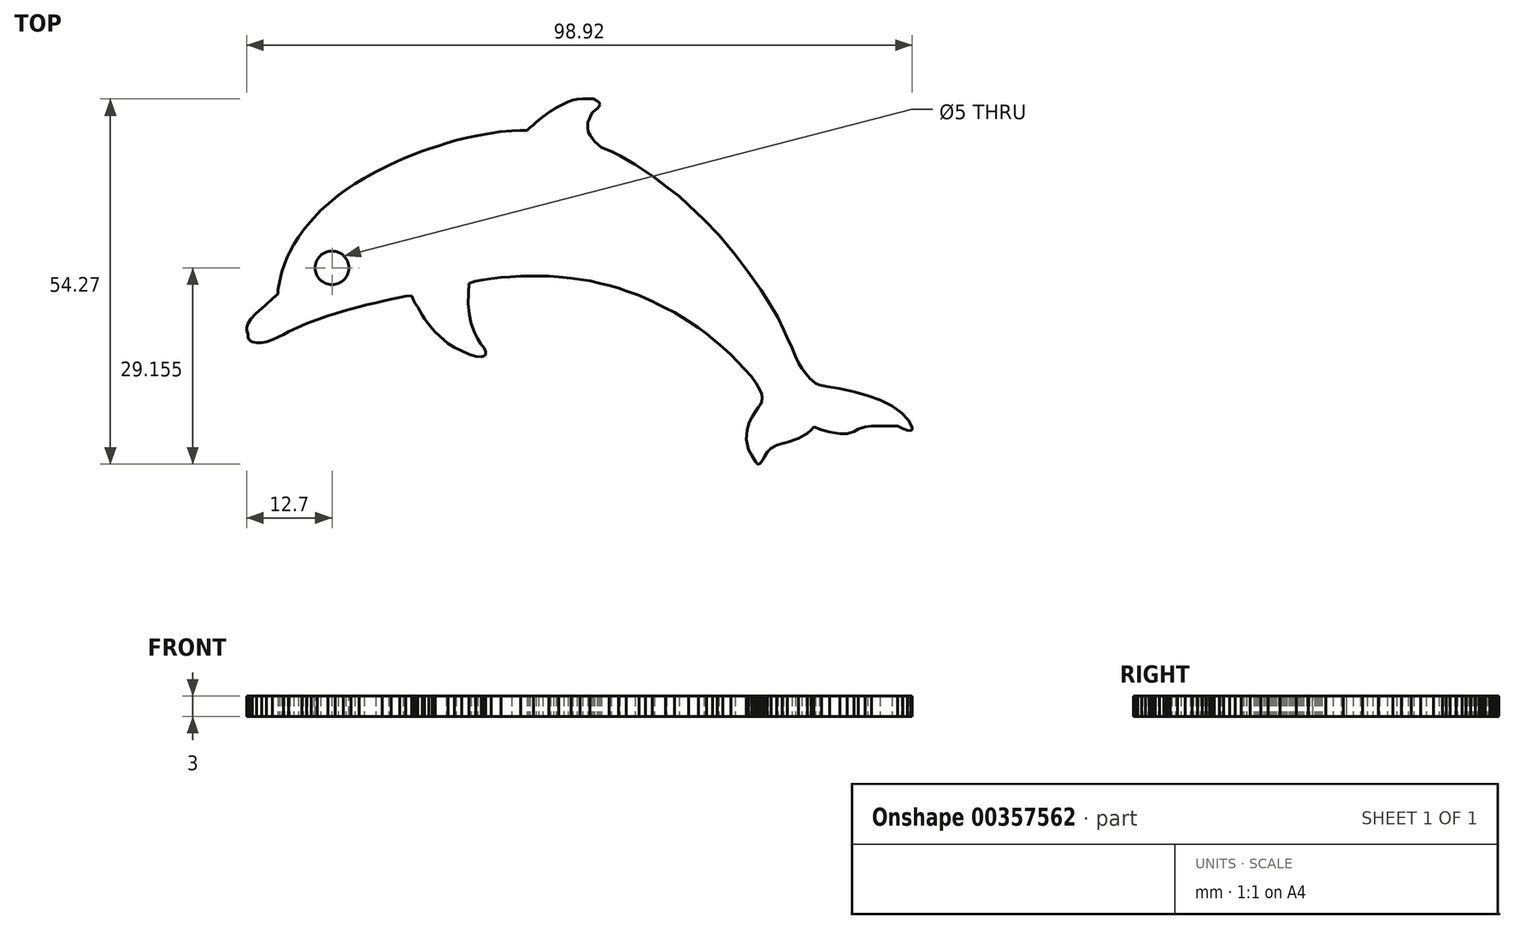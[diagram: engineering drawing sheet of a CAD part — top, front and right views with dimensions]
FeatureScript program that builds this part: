
annotation { "Feature Type Name" : "Feature", "Feature Type Description" : "" }
export const myFeature = defineFeature(function(context is Context, id is Id, definition is map)
    precondition{}
    {
        {
            var Q0;
            Q0=qCreatedBy(makeId("Top.planeOp"),FACE);
            var sketch = newSketch(context, id + "F0", { "sketchPlane" : qUnion([Q0])});
            skLineSegment(sketch, "E0.bottom", {"start": v(0, 0) * mm, "end": v(-99.99, 0) * mm});
            skLineSegment(sketch, "E1", {"start": v(-15.33, 6.38) * mm, "end": v(-14.23, 5.94) * mm});
            skLineSegment(sketch, "E2", {"start": v(-14.23, 5.94) * mm, "end": v(-13.02, 5.63) * mm});
            skLineSegment(sketch, "E3", {"start": v(-13.02, 5.63) * mm, "end": v(-11.47, 5.39) * mm});
            skLineSegment(sketch, "E4", {"start": v(-11.47, 5.39) * mm, "end": v(-10.37, 5.39) * mm});
            skLineSegment(sketch, "E5", {"start": v(-10.37, 5.39) * mm, "end": v(-9.38, 5.72) * mm});
            skLineSegment(sketch, "E6", {"start": v(-9.38, 5.72) * mm, "end": v(-8.72, 6.1) * mm});
            skLineSegment(sketch, "E7", {"start": v(-8.72, 6.1) * mm, "end": v(-7.72, 6.4) * mm});
            skLineSegment(sketch, "E8", {"start": v(-7.72, 6.4) * mm, "end": v(-6.76, 6.54) * mm});
            skLineSegment(sketch, "E9", {"start": v(-6.76, 6.54) * mm, "end": v(-5.65, 6.54) * mm});
            skLineSegment(sketch, "E10", {"start": v(-5.65, 6.54) * mm, "end": v(-2.9, 6.54) * mm});
            skPoint(sketch, "E10.endSnap0", {"position": v(-6.2, 6.54) * mm});
            skLineSegment(sketch, "E11", {"start": v(-2.9, 6.54) * mm, "end": v(-2.14, 6.17) * mm});
            skLineSegment(sketch, "E12", {"start": v(-2.14, 6.17) * mm, "end": v(-1.43, 5.9) * mm});
            skLineSegment(sketch, "E13", {"start": v(-1.43, 5.9) * mm, "end": v(-0.96, 5.8) * mm});
            skLineSegment(sketch, "E14", {"start": v(-0.96, 5.8) * mm, "end": v(-0.72, 5.96) * mm});
            skLineSegment(sketch, "E15", {"start": v(-0.72, 5.96) * mm, "end": v(-0.72, 6.33) * mm});
            skLineSegment(sketch, "E16", {"start": v(-0.72, 6.33) * mm, "end": v(-1.34, 7.4) * mm});
            skLineSegment(sketch, "E17", {"start": v(-1.34, 7.4) * mm, "end": v(-2.34, 8.52) * mm});
            skLineSegment(sketch, "E18", {"start": v(-2.34, 8.52) * mm, "end": v(-3.76, 9.53) * mm});
            skLineSegment(sketch, "E19", {"start": v(-3.76, 9.53) * mm, "end": v(-5.5, 10.4) * mm});
            skLineSegment(sketch, "E20", {"start": v(-5.5, 10.4) * mm, "end": v(-7.33, 11.05) * mm});
            skLineSegment(sketch, "E21", {"start": v(-7.33, 11.05) * mm, "end": v(-9.32, 11.63) * mm});
            skLineSegment(sketch, "E22", {"start": v(-9.32, 11.63) * mm, "end": v(-11.6, 12.13) * mm});
            skLineSegment(sketch, "E23", {"start": v(-11.6, 12.13) * mm, "end": v(-13.27, 12.4) * mm});
            skLineSegment(sketch, "E24", {"start": v(-13.27, 12.4) * mm, "end": v(-14.54, 12.6) * mm});
            skLineSegment(sketch, "E25", {"start": v(-14.54, 12.6) * mm, "end": v(-15.08, 12.86) * mm});
            skLineSegment(sketch, "E26", {"start": v(-15.08, 12.86) * mm, "end": v(-15.9, 13.6) * mm});
            skLineSegment(sketch, "E27", {"start": v(-15.9, 13.6) * mm, "end": v(-16.5, 14.26) * mm});
            skLineSegment(sketch, "E28", {"start": v(-16.5, 14.26) * mm, "end": v(-17.1, 15.11) * mm});
            skLineSegment(sketch, "E29", {"start": v(-17.1, 15.11) * mm, "end": v(-17.61, 15.95) * mm});
            skLineSegment(sketch, "E30", {"start": v(-17.61, 15.95) * mm, "end": v(-18.05, 16.88) * mm});
            skLineSegment(sketch, "E31", {"start": v(-18.05, 16.88) * mm, "end": v(-18.59, 18.16) * mm});
            skLineSegment(sketch, "E32", {"start": v(-18.59, 18.16) * mm, "end": v(-19.32, 19.77) * mm});
            skLineSegment(sketch, "E33", {"start": v(-19.32, 19.77) * mm, "end": v(-19.89, 20.87) * mm});
            skLineSegment(sketch, "E34", {"start": v(-19.89, 20.87) * mm, "end": v(-20.7, 22.66) * mm});
            skLineSegment(sketch, "E35", {"start": v(-20.7, 22.66) * mm, "end": v(-22.15, 25.05) * mm});
            skLineSegment(sketch, "E36", {"start": v(-22.15, 25.05) * mm, "end": v(-23.23, 26.8) * mm});
            skLineSegment(sketch, "E37", {"start": v(-23.23, 26.8) * mm, "end": v(-25.1, 29.44) * mm});
            skLineSegment(sketch, "E38", {"start": v(-25.1, 29.44) * mm, "end": v(-27, 32.02) * mm});
            skLineSegment(sketch, "E39", {"start": v(-27, 32.02) * mm, "end": v(-29.44, 34.91) * mm});
            skLineSegment(sketch, "E40", {"start": v(-29.44, 34.91) * mm, "end": v(-31.68, 37.22) * mm});
            skLineSegment(sketch, "E41", {"start": v(-31.68, 37.22) * mm, "end": v(-33.94, 39.38) * mm});
            skLineSegment(sketch, "E42", {"start": v(-33.94, 39.38) * mm, "end": v(-35.38, 40.67) * mm});
            skLineSegment(sketch, "E43", {"start": v(-35.38, 40.67) * mm, "end": v(-37.23, 42.1) * mm});
            skLineSegment(sketch, "E44", {"start": v(-37.23, 42.1) * mm, "end": v(-39, 43.51) * mm});
            skLineSegment(sketch, "E45", {"start": v(-39, 43.51) * mm, "end": v(-41.91, 45.4) * mm});
            skLineSegment(sketch, "E46", {"start": v(-41.91, 45.4) * mm, "end": v(-44.16, 46.74) * mm});
            skLineSegment(sketch, "E47", {"start": v(-44.16, 46.74) * mm, "end": v(-45.42, 47.36) * mm});
            skLineSegment(sketch, "E48", {"start": v(-45.42, 47.36) * mm, "end": v(-46.9, 47.9) * mm});
            skLineSegment(sketch, "E49", {"start": v(-46.9, 47.9) * mm, "end": v(-47.92, 48.82) * mm});
            skLineSegment(sketch, "E50", {"start": v(-47.92, 48.82) * mm, "end": v(-48.58, 49.7) * mm});
            skLineSegment(sketch, "E51", {"start": v(-48.58, 49.7) * mm, "end": v(-48.85, 50.24) * mm});
            skLineSegment(sketch, "E52", {"start": v(-48.85, 50.24) * mm, "end": v(-48.95, 50.93) * mm});
            skLineSegment(sketch, "E53", {"start": v(-48.95, 50.93) * mm, "end": v(-48.91, 51.65) * mm});
            skLineSegment(sketch, "E54", {"start": v(-48.91, 51.65) * mm, "end": v(-48.7, 52.21) * mm});
            skLineSegment(sketch, "E55", {"start": v(-48.7, 52.21) * mm, "end": v(-48.48, 52.68) * mm});
            skLineSegment(sketch, "E56", {"start": v(-48.48, 52.68) * mm, "end": v(-48.22, 53.11) * mm});
            skLineSegment(sketch, "E57", {"start": v(-48.22, 53.11) * mm, "end": v(-47.87, 53.43) * mm});
            skLineSegment(sketch, "E58", {"start": v(-47.87, 53.43) * mm, "end": v(-47.48, 53.79) * mm});
            skLineSegment(sketch, "E59", {"start": v(-47.48, 53.79) * mm, "end": v(-47.23, 54.06) * mm});
            skLineSegment(sketch, "E60", {"start": v(-47.23, 54.06) * mm, "end": v(-47.19, 54.33) * mm});
            skLineSegment(sketch, "E61", {"start": v(-47.19, 54.33) * mm, "end": v(-47.23, 54.62) * mm});
            skLineSegment(sketch, "E62", {"start": v(-47.23, 54.62) * mm, "end": v(-47.53, 54.85) * mm});
            skLineSegment(sketch, "E63", {"start": v(-47.53, 54.85) * mm, "end": v(-48.14, 55.15) * mm});
            skLineSegment(sketch, "E64", {"start": v(-48.14, 55.15) * mm, "end": v(-48.9, 55.15) * mm});
            skLineSegment(sketch, "E65", {"start": v(-48.9, 55.15) * mm, "end": v(-49.68, 55.15) * mm});
            skLineSegment(sketch, "E66", {"start": v(-49.68, 55.15) * mm, "end": v(-50.55, 55.09) * mm});
            skLineSegment(sketch, "E67", {"start": v(-50.55, 55.09) * mm, "end": v(-51.18, 54.95) * mm});
            skLineSegment(sketch, "E68", {"start": v(-51.18, 54.95) * mm, "end": v(-51.84, 54.73) * mm});
            skLineSegment(sketch, "E69", {"start": v(-51.84, 54.73) * mm, "end": v(-52.48, 54.44) * mm});
            skLineSegment(sketch, "E70", {"start": v(-52.48, 54.44) * mm, "end": v(-53.11, 54.12) * mm});
            skLineSegment(sketch, "E71", {"start": v(-53.11, 54.12) * mm, "end": v(-53.63, 53.85) * mm});
            skLineSegment(sketch, "E72", {"start": v(-53.63, 53.85) * mm, "end": v(-54.03, 53.6) * mm});
            skLineSegment(sketch, "E73", {"start": v(-54.03, 53.6) * mm, "end": v(-54.45, 53.35) * mm});
            skLineSegment(sketch, "E74", {"start": v(-54.45, 53.35) * mm, "end": v(-54.7, 53.17) * mm});
            skLineSegment(sketch, "E75", {"start": v(-54.7, 53.17) * mm, "end": v(-55.04, 52.92) * mm});
            skLineSegment(sketch, "E76", {"start": v(-55.04, 52.92) * mm, "end": v(-55.31, 52.72) * mm});
            skLineSegment(sketch, "E77", {"start": v(-55.31, 52.72) * mm, "end": v(-55.62, 52.49) * mm});
            skLineSegment(sketch, "E78", {"start": v(-55.62, 52.49) * mm, "end": v(-55.88, 52.27) * mm});
            skLineSegment(sketch, "E79", {"start": v(-55.88, 52.27) * mm, "end": v(-56.22, 51.98) * mm});
            skLineSegment(sketch, "E80", {"start": v(-56.22, 51.98) * mm, "end": v(-56.61, 51.68) * mm});
            skLineSegment(sketch, "E81", {"start": v(-56.61, 51.68) * mm, "end": v(-57.08, 51.25) * mm});
            skLineSegment(sketch, "E82", {"start": v(-57.08, 51.25) * mm, "end": v(-57.5, 50.92) * mm});
            skLineSegment(sketch, "E83", {"start": v(-57.5, 50.92) * mm, "end": v(-57.76, 50.63) * mm});
            skLineSegment(sketch, "E84", {"start": v(-57.76, 50.63) * mm, "end": v(-57.98, 50.47) * mm});
            skLineSegment(sketch, "E85", {"start": v(-57.98, 50.47) * mm, "end": v(-59.07, 50.47) * mm});
            skLineSegment(sketch, "E86", {"start": v(-59.07, 50.47) * mm, "end": v(-60.22, 50.39) * mm});
            skLineSegment(sketch, "E87", {"start": v(-60.22, 50.39) * mm, "end": v(-61.94, 50.28) * mm});
            skLineSegment(sketch, "E88", {"start": v(-61.94, 50.28) * mm, "end": v(-63.42, 50.05) * mm});
            skLineSegment(sketch, "E89", {"start": v(-63.42, 50.05) * mm, "end": v(-65.27, 49.74) * mm});
            skLineSegment(sketch, "E90", {"start": v(-65.27, 49.74) * mm, "end": v(-66.86, 49.37) * mm});
            skLineSegment(sketch, "E91", {"start": v(-66.86, 49.37) * mm, "end": v(-68.52, 48.98) * mm});
            skLineSegment(sketch, "E92", {"start": v(-68.52, 48.98) * mm, "end": v(-69.93, 48.57) * mm});
            skLineSegment(sketch, "E93", {"start": v(-69.93, 48.57) * mm, "end": v(-71.05, 48.2) * mm});
            skLineSegment(sketch, "E94", {"start": v(-71.05, 48.2) * mm, "end": v(-72.49, 47.73) * mm});
            skLineSegment(sketch, "E95", {"start": v(-72.49, 47.73) * mm, "end": v(-73.62, 47.33) * mm});
            skLineSegment(sketch, "E96", {"start": v(-73.62, 47.33) * mm, "end": v(-74.6, 46.98) * mm});
            skLineSegment(sketch, "E97", {"start": v(-74.6, 46.98) * mm, "end": v(-76.39, 46.28) * mm});
            skLineSegment(sketch, "E98", {"start": v(-76.39, 46.28) * mm, "end": v(-78.55, 45.28) * mm});
            skLineSegment(sketch, "E99", {"start": v(-78.55, 45.28) * mm, "end": v(-80.45, 44.34) * mm});
            skLineSegment(sketch, "E100", {"start": v(-80.45, 44.34) * mm, "end": v(-82.14, 43.39) * mm});
            skLineSegment(sketch, "E101", {"start": v(-82.14, 43.39) * mm, "end": v(-83.57, 42.53) * mm});
            skLineSegment(sketch, "E102", {"start": v(-83.57, 42.53) * mm, "end": v(-84.85, 41.65) * mm});
            skLineSegment(sketch, "E103", {"start": v(-84.85, 41.65) * mm, "end": v(-86.03, 40.79) * mm});
            skLineSegment(sketch, "E104", {"start": v(-86.03, 40.79) * mm, "end": v(-87, 40) * mm});
            skLineSegment(sketch, "E105", {"start": v(-87, 40) * mm, "end": v(-88.63, 38.57) * mm});
            skLineSegment(sketch, "E106", {"start": v(-88.63, 38.57) * mm, "end": v(-89.65, 37.44) * mm});
            skLineSegment(sketch, "E107", {"start": v(-89.65, 37.44) * mm, "end": v(-90.61, 36.4) * mm});
            skLineSegment(sketch, "E108", {"start": v(-90.61, 36.4) * mm, "end": v(-91.23, 35.6) * mm});
            skLineSegment(sketch, "E109", {"start": v(-91.23, 35.6) * mm, "end": v(-91.94, 34.6) * mm});
            skLineSegment(sketch, "E110", {"start": v(-91.94, 34.6) * mm, "end": v(-92.6, 33.5) * mm});
            skLineSegment(sketch, "E111", {"start": v(-92.6, 33.5) * mm, "end": v(-93.2, 32.44) * mm});
            skLineSegment(sketch, "E112", {"start": v(-93.2, 32.44) * mm, "end": v(-93.6, 31.7) * mm});
            skLineSegment(sketch, "E113", {"start": v(-93.6, 31.7) * mm, "end": v(-94.03, 30.52) * mm});
            skLineSegment(sketch, "E114", {"start": v(-94.03, 30.52) * mm, "end": v(-94.38, 29.46) * mm});
            skLineSegment(sketch, "E115", {"start": v(-94.38, 29.46) * mm, "end": v(-94.72, 28) * mm});
            skLineSegment(sketch, "E116", {"start": v(-94.72, 28) * mm, "end": v(-95, 26.76) * mm});
            skLineSegment(sketch, "E117", {"start": v(-95, 26.76) * mm, "end": v(-95, 26.14) * mm});
            skLineSegment(sketch, "E118", {"start": v(-95, 26.14) * mm, "end": v(-95.71, 25.52) * mm});
            skLineSegment(sketch, "E119", {"start": v(-95.71, 25.52) * mm, "end": v(-96.82, 24.48) * mm});
            skLineSegment(sketch, "E120", {"start": v(-96.82, 24.48) * mm, "end": v(-98.25, 23.22) * mm});
            skLineSegment(sketch, "E121", {"start": v(-98.25, 23.22) * mm, "end": v(-98.96, 22.45) * mm});
            skLineSegment(sketch, "E122", {"start": v(-98.96, 22.45) * mm, "end": v(-99.43, 21.76) * mm});
            skLineSegment(sketch, "E123", {"start": v(-99.43, 21.76) * mm, "end": v(-99.55, 21.39) * mm});
            skLineSegment(sketch, "E124", {"start": v(-99.55, 21.39) * mm, "end": v(-99.64, 21.11) * mm});
            skLineSegment(sketch, "E125", {"start": v(-99.64, 21.11) * mm, "end": v(-99.6, 20.62) * mm});
            skLineSegment(sketch, "E126", {"start": v(-99.6, 20.62) * mm, "end": v(-99.44, 20.28) * mm});
            skLineSegment(sketch, "E127", {"start": v(-99.44, 20.28) * mm, "end": v(-99.44, 19.73) * mm});
            skLineSegment(sketch, "E128", {"start": v(-99.44, 19.73) * mm, "end": v(-99.2, 19.31) * mm});
            skLineSegment(sketch, "E129", {"start": v(-99.2, 19.31) * mm, "end": v(-98.77, 19.02) * mm});
            skLineSegment(sketch, "E130", {"start": v(-98.77, 19.02) * mm, "end": v(-98.13, 18.9) * mm});
            skLineSegment(sketch, "E131", {"start": v(-98.13, 18.9) * mm, "end": v(-97.38, 18.9) * mm});
            skLineSegment(sketch, "E132", {"start": v(-97.38, 18.9) * mm, "end": v(-96.72, 19.05) * mm});
            skLineSegment(sketch, "E133", {"start": v(-96.72, 19.05) * mm, "end": v(-95.84, 19.36) * mm});
            skLineSegment(sketch, "E134", {"start": v(-95.84, 19.36) * mm, "end": v(-95.07, 19.72) * mm});
            skLineSegment(sketch, "E135", {"start": v(-95.07, 19.72) * mm, "end": v(-94.18, 20.12) * mm});
            skLineSegment(sketch, "E136", {"start": v(-94.18, 20.12) * mm, "end": v(-93.4, 20.56) * mm});
            skLineSegment(sketch, "E137", {"start": v(-93.4, 20.56) * mm, "end": v(-92.8, 20.84) * mm});
            skLineSegment(sketch, "E138", {"start": v(-92.8, 20.84) * mm, "end": v(-92.09, 21.16) * mm});
            skLineSegment(sketch, "E139", {"start": v(-92.09, 21.16) * mm, "end": v(-91.4, 21.47) * mm});
            skLineSegment(sketch, "E140", {"start": v(-91.4, 21.47) * mm, "end": v(-90.72, 21.76) * mm});
            skLineSegment(sketch, "E141", {"start": v(-90.72, 21.76) * mm, "end": v(-90.01, 22.01) * mm});
            skLineSegment(sketch, "E142", {"start": v(-90.01, 22.01) * mm, "end": v(-89.13, 22.36) * mm});
            skLineSegment(sketch, "E143", {"start": v(-89.13, 22.36) * mm, "end": v(-88.18, 22.7) * mm});
            skLineSegment(sketch, "E144", {"start": v(-88.18, 22.7) * mm, "end": v(-87.55, 22.92) * mm});
            skLineSegment(sketch, "E145", {"start": v(-87.55, 22.92) * mm, "end": v(-86.44, 23.25) * mm});
            skLineSegment(sketch, "E146", {"start": v(-86.44, 23.25) * mm, "end": v(-85.25, 23.62) * mm});
            skLineSegment(sketch, "E147", {"start": v(-85.25, 23.62) * mm, "end": v(-84.14, 23.94) * mm});
            skLineSegment(sketch, "E148", {"start": v(-84.14, 23.94) * mm, "end": v(-82.92, 24.26) * mm});
            skLineSegment(sketch, "E149", {"start": v(-82.92, 24.26) * mm, "end": v(-81.76, 24.53) * mm});
            skLineSegment(sketch, "E150", {"start": v(-81.76, 24.53) * mm, "end": v(-80.5, 24.84) * mm});
            skLineSegment(sketch, "E151", {"start": v(-80.5, 24.84) * mm, "end": v(-79.51, 25.08) * mm});
            skLineSegment(sketch, "E152", {"start": v(-79.51, 25.08) * mm, "end": v(-78.15, 25.4) * mm});
            skLineSegment(sketch, "E153", {"start": v(-78.15, 25.4) * mm, "end": v(-76.89, 25.65) * mm});
            skLineSegment(sketch, "E154", {"start": v(-76.89, 25.65) * mm, "end": v(-75.98, 25.82) * mm});
            skLineSegment(sketch, "E155", {"start": v(-75.98, 25.82) * mm, "end": v(-75.1, 25.93) * mm});
            skLineSegment(sketch, "E156", {"start": v(-75.1, 25.93) * mm, "end": v(-74.85, 25.25) * mm});
            skLineSegment(sketch, "E157", {"start": v(-74.85, 25.25) * mm, "end": v(-74.57, 24.75) * mm});
            skLineSegment(sketch, "E158", {"start": v(-74.57, 24.75) * mm, "end": v(-74.23, 24.25) * mm});
            skLineSegment(sketch, "E159", {"start": v(-74.23, 24.25) * mm, "end": v(-73.91, 23.7) * mm});
            skLineSegment(sketch, "E160", {"start": v(-73.91, 23.7) * mm, "end": v(-73.52, 23) * mm});
            skLineSegment(sketch, "E161", {"start": v(-73.52, 23) * mm, "end": v(-73.17, 22.49) * mm});
            skLineSegment(sketch, "E162", {"start": v(-73.17, 22.49) * mm, "end": v(-72.84, 22.04) * mm});
            skLineSegment(sketch, "E163", {"start": v(-72.84, 22.04) * mm, "end": v(-72.56, 21.65) * mm});
            skLineSegment(sketch, "E164", {"start": v(-72.56, 21.65) * mm, "end": v(-72.03, 20.98) * mm});
            skLineSegment(sketch, "E165", {"start": v(-72.03, 20.98) * mm, "end": v(-71.6, 20.53) * mm});
            skLineSegment(sketch, "E166", {"start": v(-71.6, 20.53) * mm, "end": v(-71.02, 19.98) * mm});
            skLineSegment(sketch, "E167", {"start": v(-71.02, 19.98) * mm, "end": v(-70.31, 19.32) * mm});
            skLineSegment(sketch, "E168", {"start": v(-70.31, 19.32) * mm, "end": v(-69.72, 18.78) * mm});
            skLineSegment(sketch, "E169", {"start": v(-69.72, 18.78) * mm, "end": v(-68.76, 18.23) * mm});
            skLineSegment(sketch, "E170", {"start": v(-68.76, 18.23) * mm, "end": v(-67.65, 17.7) * mm});
            skLineSegment(sketch, "E171", {"start": v(-67.65, 17.7) * mm, "end": v(-66.57, 17.21) * mm});
            skLineSegment(sketch, "E172", {"start": v(-66.57, 17.21) * mm, "end": v(-65.59, 16.88) * mm});
            skLineSegment(sketch, "E173", {"start": v(-65.59, 16.88) * mm, "end": v(-64.77, 16.8) * mm});
            skLineSegment(sketch, "E174", {"start": v(-64.77, 16.8) * mm, "end": v(-64.36, 16.91) * mm});
            skLineSegment(sketch, "E175", {"start": v(-64.36, 16.91) * mm, "end": v(-64.13, 17.15) * mm});
            skLineSegment(sketch, "E176", {"start": v(-64.13, 17.15) * mm, "end": v(-64.13, 17.59) * mm});
            skLineSegment(sketch, "E177", {"start": v(-64.13, 17.59) * mm, "end": v(-64.32, 18.1) * mm});
            skLineSegment(sketch, "E178", {"start": v(-64.32, 18.1) * mm, "end": v(-64.89, 18.76) * mm});
            skLineSegment(sketch, "E179", {"start": v(-64.89, 18.76) * mm, "end": v(-65.34, 19.56) * mm});
            skLineSegment(sketch, "E180", {"start": v(-65.34, 19.56) * mm, "end": v(-65.73, 20.41) * mm});
            skLineSegment(sketch, "E181", {"start": v(-65.73, 20.41) * mm, "end": v(-66.29, 21.78) * mm});
            skLineSegment(sketch, "E182", {"start": v(-66.29, 21.78) * mm, "end": v(-66.56, 23.11) * mm});
            skLineSegment(sketch, "E183", {"start": v(-66.56, 23.11) * mm, "end": v(-66.7, 24.78) * mm});
            skLineSegment(sketch, "E184", {"start": v(-66.7, 24.78) * mm, "end": v(-66.57, 27.77) * mm});
            skLineSegment(sketch, "E185", {"start": v(-66.57, 27.77) * mm, "end": v(-65.66, 28.03) * mm});
            skLineSegment(sketch, "E186", {"start": v(-65.66, 28.03) * mm, "end": v(-64.55, 28.24) * mm});
            skLineSegment(sketch, "E187", {"start": v(-64.55, 28.24) * mm, "end": v(-63.27, 28.44) * mm});
            skLineSegment(sketch, "E188", {"start": v(-63.27, 28.44) * mm, "end": v(-61.84, 28.6) * mm});
            skLineSegment(sketch, "E189", {"start": v(-61.84, 28.6) * mm, "end": v(-60.48, 28.7) * mm});
            skLineSegment(sketch, "E190", {"start": v(-60.48, 28.7) * mm, "end": v(-58.9, 28.83) * mm});
            skLineSegment(sketch, "E191", {"start": v(-58.9, 28.83) * mm, "end": v(-57, 28.83) * mm});
            skLineSegment(sketch, "E192", {"start": v(-57, 28.83) * mm, "end": v(-54.74, 28.8) * mm});
            skLineSegment(sketch, "E193", {"start": v(-54.74, 28.8) * mm, "end": v(-53.23, 28.7) * mm});
            skLineSegment(sketch, "E194", {"start": v(-53.23, 28.7) * mm, "end": v(-51.42, 28.53) * mm});
            skLineSegment(sketch, "E195", {"start": v(-51.42, 28.53) * mm, "end": v(-50.07, 28.3) * mm});
            skLineSegment(sketch, "E196", {"start": v(-50.07, 28.3) * mm, "end": v(-48.62, 28.09) * mm});
            skLineSegment(sketch, "E197", {"start": v(-48.62, 28.09) * mm, "end": v(-47.14, 27.73) * mm});
            skLineSegment(sketch, "E198", {"start": v(-47.14, 27.73) * mm, "end": v(-45.78, 27.4) * mm});
            skLineSegment(sketch, "E199", {"start": v(-45.78, 27.4) * mm, "end": v(-44.35, 27.01) * mm});
            skLineSegment(sketch, "E200", {"start": v(-44.35, 27.01) * mm, "end": v(-43.24, 26.57) * mm});
            skLineSegment(sketch, "E201", {"start": v(-43.24, 26.57) * mm, "end": v(-42.47, 26.32) * mm});
            skLineSegment(sketch, "E202", {"start": v(-42.47, 26.32) * mm, "end": v(-41.31, 25.93) * mm});
            skLineSegment(sketch, "E203", {"start": v(-41.31, 25.93) * mm, "end": v(-40.37, 25.54) * mm});
            skLineSegment(sketch, "E204", {"start": v(-40.37, 25.54) * mm, "end": v(-39.38, 25.08) * mm});
            skLineSegment(sketch, "E205", {"start": v(-39.38, 25.08) * mm, "end": v(-38.64, 24.7) * mm});
            skLineSegment(sketch, "E206", {"start": v(-38.64, 24.7) * mm, "end": v(-37.4, 24.08) * mm});
            skLineSegment(sketch, "E207", {"start": v(-37.4, 24.08) * mm, "end": v(-36.06, 23.4) * mm});
            skLineSegment(sketch, "E208", {"start": v(-36.06, 23.4) * mm, "end": v(-34.84, 22.64) * mm});
            skLineSegment(sketch, "E209", {"start": v(-34.84, 22.64) * mm, "end": v(-33.94, 22.08) * mm});
            skLineSegment(sketch, "E210", {"start": v(-33.94, 22.08) * mm, "end": v(-33.15, 21.54) * mm});
            skLineSegment(sketch, "E211", {"start": v(-33.15, 21.54) * mm, "end": v(-32.5, 21.1) * mm});
            skLineSegment(sketch, "E212", {"start": v(-32.5, 21.1) * mm, "end": v(-31.31, 20.25) * mm});
            skLineSegment(sketch, "E213", {"start": v(-31.31, 20.25) * mm, "end": v(-30.37, 19.5) * mm});
            skLineSegment(sketch, "E214", {"start": v(-30.37, 19.5) * mm, "end": v(-29.7, 18.88) * mm});
            skLineSegment(sketch, "E215", {"start": v(-29.7, 18.88) * mm, "end": v(-28.9, 18.23) * mm});
            skLineSegment(sketch, "E216", {"start": v(-28.9, 18.23) * mm, "end": v(-28.44, 17.81) * mm});
            skLineSegment(sketch, "E217", {"start": v(-28.44, 17.81) * mm, "end": v(-27.68, 17.1) * mm});
            skLineSegment(sketch, "E218", {"start": v(-27.68, 17.1) * mm, "end": v(-26.84, 16.22) * mm});
            skLineSegment(sketch, "E219", {"start": v(-26.84, 16.22) * mm, "end": v(-26.06, 15.38) * mm});
            skLineSegment(sketch, "E220", {"start": v(-26.06, 15.38) * mm, "end": v(-25.3, 14.58) * mm});
            skLineSegment(sketch, "E221", {"start": v(-25.3, 14.58) * mm, "end": v(-24.64, 13.89) * mm});
            skLineSegment(sketch, "E222", {"start": v(-24.64, 13.89) * mm, "end": v(-23.93, 12.85) * mm});
            skLineSegment(sketch, "E223", {"start": v(-23.93, 12.85) * mm, "end": v(-23.37, 11.84) * mm});
            skLineSegment(sketch, "E224", {"start": v(-23.37, 11.84) * mm, "end": v(-23.1, 11.27) * mm});
            skLineSegment(sketch, "E225", {"start": v(-23.1, 11.27) * mm, "end": v(-23.03, 10.73) * mm});
            skLineSegment(sketch, "E226", {"start": v(-23.03, 10.73) * mm, "end": v(-23.07, 10.12) * mm});
            skPoint(sketch, "E226.endSnap0", {"position": v(-23.07, 11) * mm});
            skLineSegment(sketch, "E227", {"start": v(-23.07, 10.12) * mm, "end": v(-23.29, 9.73) * mm});
            skLineSegment(sketch, "E228", {"start": v(-23.29, 9.73) * mm, "end": v(-23.61, 9.32) * mm});
            skLineSegment(sketch, "E229", {"start": v(-23.61, 9.32) * mm, "end": v(-23.94, 8.78) * mm});
            skLineSegment(sketch, "E230", {"start": v(-23.94, 8.78) * mm, "end": v(-24.48, 7.92) * mm});
            skLineSegment(sketch, "E231", {"start": v(-24.48, 7.92) * mm, "end": v(-24.96, 7.07) * mm});
            skLineSegment(sketch, "E232", {"start": v(-24.96, 7.07) * mm, "end": v(-25.26, 5.96) * mm});
            skLineSegment(sketch, "E233", {"start": v(-25.26, 5.96) * mm, "end": v(-25.37, 4.53) * mm});
            skLineSegment(sketch, "E234", {"start": v(-25.37, 4.53) * mm, "end": v(-25.06, 3.02) * mm});
            skLineSegment(sketch, "E235", {"start": v(-25.06, 3.02) * mm, "end": v(-24.58, 2.16) * mm});
            skLineSegment(sketch, "E236", {"start": v(-24.58, 2.16) * mm, "end": v(-24.15, 1.53) * mm});
            skLineSegment(sketch, "E237", {"start": v(-24.15, 1.53) * mm, "end": v(-23.96, 1.2) * mm});
            skLineSegment(sketch, "E238", {"start": v(-23.96, 1.2) * mm, "end": v(-23.73, 0.9) * mm});
            skLineSegment(sketch, "E239", {"start": v(-23.73, 0.9) * mm, "end": v(-23.55, 0.88) * mm});
            skLineSegment(sketch, "E240", {"start": v(-23.55, 0.88) * mm, "end": v(-23.3, 1.02) * mm});
            skLineSegment(sketch, "E241", {"start": v(-23.3, 1.02) * mm, "end": v(-22.95, 1.46) * mm});
            skLineSegment(sketch, "E242", {"start": v(-22.95, 1.46) * mm, "end": v(-22.68, 2.04) * mm});
            skLineSegment(sketch, "E243", {"start": v(-22.68, 2.04) * mm, "end": v(-22.27, 2.65) * mm});
            skLineSegment(sketch, "E244", {"start": v(-22.27, 2.65) * mm, "end": v(-21.69, 3.2) * mm});
            skLineSegment(sketch, "E245", {"start": v(-21.69, 3.2) * mm, "end": v(-20.88, 3.65) * mm});
            skLineSegment(sketch, "E246", {"start": v(-20.88, 3.65) * mm, "end": v(-20.03, 3.96) * mm});
            skLineSegment(sketch, "E247", {"start": v(-20.03, 3.96) * mm, "end": v(-19.3, 4.1) * mm});
            skLineSegment(sketch, "E248", {"start": v(-19.3, 4.1) * mm, "end": v(-18.54, 4.38) * mm});
            skLineSegment(sketch, "E249", {"start": v(-18.54, 4.38) * mm, "end": v(-17.63, 4.7) * mm});
            skLineSegment(sketch, "E250", {"start": v(-17.63, 4.7) * mm, "end": v(-16.97, 5.07) * mm});
            skLineSegment(sketch, "E251", {"start": v(-16.97, 5.07) * mm, "end": v(-16.33, 5.43) * mm});
            skLineSegment(sketch, "E252", {"start": v(-16.33, 5.43) * mm, "end": v(-15.73, 5.96) * mm});
            skLineSegment(sketch, "E253", {"start": v(-15.73, 5.96) * mm, "end": v(-15.33, 6.38) * mm});
            skSolve(sketch);
        }
        {
            var Q0;
            Q0=makeQuery(id+"F0.imprint","IMPRINT",FACE,{"disambiguationData":[TD([[makeQuery(id+"F0.imprint","IMPRINT",EDGE,{"derivedFrom":sQuery(id+"F0.wireOp",EDGE,"E1")}),1.0]])]});
            extrude(context, id + "F1", {"entities" : qUnion([Q0]), "depth" : 3 * mm});
        }
        {
            var Q0;
            {var subQ0=sQuery(id+"F0.wireOp",EDGE,"E215");var subQ1=sQuery(id+"F0.wireOp",EDGE,"E214");var subQ2=sQuery(id+"F0.wireOp",EDGE,"E213");var subQ3=sQuery(id+"F0.wireOp",EDGE,"E212");var subQ4=sQuery(id+"F0.wireOp",EDGE,"E211");var subQ5=sQuery(id+"F0.wireOp",EDGE,"E210");var subQ6=sQuery(id+"F0.wireOp",EDGE,"E209");var subQ7=sQuery(id+"F0.wireOp",EDGE,"E208");var subQ8=sQuery(id+"F0.wireOp",EDGE,"E207");var subQ9=sQuery(id+"F0.wireOp",EDGE,"E206");var subQ10=sQuery(id+"F0.wireOp",EDGE,"E205");var subQ11=sQuery(id+"F0.wireOp",EDGE,"E204");var subQ12=sQuery(id+"F0.wireOp",EDGE,"E203");var subQ13=sQuery(id+"F0.wireOp",EDGE,"E202");var subQ14=sQuery(id+"F0.wireOp",EDGE,"E201");var subQ15=sQuery(id+"F0.wireOp",EDGE,"E200");var subQ16=sQuery(id+"F0.wireOp",EDGE,"E199");var subQ17=sQuery(id+"F0.wireOp",EDGE,"E198");var subQ18=sQuery(id+"F0.wireOp",EDGE,"E197");var subQ19=sQuery(id+"F0.wireOp",EDGE,"E196");var subQ20=sQuery(id+"F0.wireOp",EDGE,"E195");var subQ21=sQuery(id+"F0.wireOp",EDGE,"E194");var subQ22=sQuery(id+"F0.wireOp",EDGE,"E193");var subQ23=sQuery(id+"F0.wireOp",EDGE,"E192");var subQ24=sQuery(id+"F0.wireOp",EDGE,"E191");var subQ25=sQuery(id+"F0.wireOp",EDGE,"E190");var subQ26=sQuery(id+"F0.wireOp",EDGE,"E189");var subQ27=sQuery(id+"F0.wireOp",EDGE,"E188");var subQ28=sQuery(id+"F0.wireOp",EDGE,"E187");var subQ29=sQuery(id+"F0.wireOp",EDGE,"E186");var subQ30=sQuery(id+"F0.wireOp",EDGE,"E185");var subQ31=sQuery(id+"F0.wireOp",EDGE,"E184");var subQ32=sQuery(id+"F0.wireOp",EDGE,"E183");var subQ33=sQuery(id+"F0.wireOp",EDGE,"E182");var subQ34=sQuery(id+"F0.wireOp",EDGE,"E181");var subQ35=sQuery(id+"F0.wireOp",EDGE,"E180");var subQ36=sQuery(id+"F0.wireOp",EDGE,"E179");var subQ37=sQuery(id+"F0.wireOp",EDGE,"E178");var subQ38=sQuery(id+"F0.wireOp",EDGE,"E177");var subQ39=sQuery(id+"F0.wireOp",EDGE,"E176");var subQ40=sQuery(id+"F0.wireOp",EDGE,"E175");var subQ41=sQuery(id+"F0.wireOp",EDGE,"E174");var subQ42=sQuery(id+"F0.wireOp",EDGE,"E173");var subQ43=sQuery(id+"F0.wireOp",EDGE,"E172");var subQ44=sQuery(id+"F0.wireOp",EDGE,"E171");var subQ45=sQuery(id+"F0.wireOp",EDGE,"E170");var subQ46=sQuery(id+"F0.wireOp",EDGE,"E169");var subQ47=sQuery(id+"F0.wireOp",EDGE,"E168");var subQ48=sQuery(id+"F0.wireOp",EDGE,"E167");var subQ49=sQuery(id+"F0.wireOp",EDGE,"E166");var subQ50=sQuery(id+"F0.wireOp",EDGE,"E165");var subQ51=sQuery(id+"F0.wireOp",EDGE,"E164");var subQ52=sQuery(id+"F0.wireOp",EDGE,"E163");var subQ53=sQuery(id+"F0.wireOp",EDGE,"E162");var subQ54=sQuery(id+"F0.wireOp",EDGE,"E161");var subQ55=sQuery(id+"F0.wireOp",EDGE,"E160");var subQ56=sQuery(id+"F0.wireOp",EDGE,"E159");var subQ57=sQuery(id+"F0.wireOp",EDGE,"E158");var subQ58=sQuery(id+"F0.wireOp",EDGE,"E157");var subQ59=sQuery(id+"F0.wireOp",EDGE,"E156");var subQ60=sQuery(id+"F0.wireOp",EDGE,"E155");var subQ61=sQuery(id+"F0.wireOp",EDGE,"E154");var subQ62=sQuery(id+"F0.wireOp",EDGE,"E153");var subQ63=sQuery(id+"F0.wireOp",EDGE,"E152");var subQ64=sQuery(id+"F0.wireOp",EDGE,"E151");var subQ65=sQuery(id+"F0.wireOp",EDGE,"E150");var subQ66=sQuery(id+"F0.wireOp",EDGE,"E149");var subQ67=sQuery(id+"F0.wireOp",EDGE,"E148");var subQ68=sQuery(id+"F0.wireOp",EDGE,"E147");var subQ69=sQuery(id+"F0.wireOp",EDGE,"E146");var subQ70=sQuery(id+"F0.wireOp",EDGE,"E145");var subQ71=sQuery(id+"F0.wireOp",EDGE,"E144");var subQ72=sQuery(id+"F0.wireOp",EDGE,"E143");var subQ73=sQuery(id+"F0.wireOp",EDGE,"E142");var subQ74=sQuery(id+"F0.wireOp",EDGE,"E141");var subQ75=sQuery(id+"F0.wireOp",EDGE,"E140");var subQ76=sQuery(id+"F0.wireOp",EDGE,"E139");var subQ77=sQuery(id+"F0.wireOp",EDGE,"E138");var subQ78=sQuery(id+"F0.wireOp",EDGE,"E137");var subQ79=sQuery(id+"F0.wireOp",EDGE,"E136");var subQ80=sQuery(id+"F0.wireOp",EDGE,"E135");var subQ81=sQuery(id+"F0.wireOp",EDGE,"E134");var subQ82=sQuery(id+"F0.wireOp",EDGE,"E133");var subQ83=sQuery(id+"F0.wireOp",EDGE,"E132");var subQ84=sQuery(id+"F0.wireOp",EDGE,"E131");var subQ85=sQuery(id+"F0.wireOp",EDGE,"E130");var subQ86=sQuery(id+"F0.wireOp",EDGE,"E129");var subQ87=sQuery(id+"F0.wireOp",EDGE,"E128");var subQ88=sQuery(id+"F0.wireOp",EDGE,"E127");var subQ89=sQuery(id+"F0.wireOp",EDGE,"E126");var subQ90=sQuery(id+"F0.wireOp",EDGE,"E125");var subQ91=sQuery(id+"F0.wireOp",EDGE,"E124");var subQ92=sQuery(id+"F0.wireOp",EDGE,"E123");var subQ93=sQuery(id+"F0.wireOp",EDGE,"E122");var subQ94=sQuery(id+"F0.wireOp",EDGE,"E121");var subQ95=sQuery(id+"F0.wireOp",EDGE,"E120");var subQ96=sQuery(id+"F0.wireOp",EDGE,"E119");var subQ97=sQuery(id+"F0.wireOp",EDGE,"E118");var subQ98=sQuery(id+"F0.wireOp",EDGE,"E117");var subQ99=sQuery(id+"F0.wireOp",EDGE,"E116");var subQ100=sQuery(id+"F0.wireOp",EDGE,"E115");var subQ101=sQuery(id+"F0.wireOp",EDGE,"E114");var subQ102=sQuery(id+"F0.wireOp",EDGE,"E113");var subQ103=sQuery(id+"F0.wireOp",EDGE,"E112");var subQ104=sQuery(id+"F0.wireOp",EDGE,"E111");var subQ105=sQuery(id+"F0.wireOp",EDGE,"E110");var subQ106=sQuery(id+"F0.wireOp",EDGE,"E109");var subQ107=sQuery(id+"F0.wireOp",EDGE,"E108");var subQ108=sQuery(id+"F0.wireOp",EDGE,"E107");var subQ109=sQuery(id+"F0.wireOp",EDGE,"E106");var subQ110=sQuery(id+"F0.wireOp",EDGE,"E105");var subQ111=sQuery(id+"F0.wireOp",EDGE,"E46");var subQ112=sQuery(id+"F0.wireOp",EDGE,"E45");var subQ113=sQuery(id+"F0.wireOp",EDGE,"E44");var subQ114=sQuery(id+"F0.wireOp",EDGE,"E43");var subQ115=sQuery(id+"F0.wireOp",EDGE,"E42");var subQ116=sQuery(id+"F0.wireOp",EDGE,"E41");var subQ117=sQuery(id+"F0.wireOp",EDGE,"E40");var subQ118=sQuery(id+"F0.wireOp",EDGE,"E39");var subQ119=sQuery(id+"F0.wireOp",EDGE,"E38");var subQ120=sQuery(id+"F0.wireOp",EDGE,"E37");var subQ121=sQuery(id+"F0.wireOp",EDGE,"E36");var subQ122=sQuery(id+"F0.wireOp",EDGE,"E35");var subQ123=sQuery(id+"F0.wireOp",EDGE,"E34");var subQ124=sQuery(id+"F0.wireOp",EDGE,"E33");var subQ125=sQuery(id+"F0.wireOp",EDGE,"E32");var subQ126=sQuery(id+"F0.wireOp",EDGE,"E31");var subQ127=sQuery(id+"F0.wireOp",EDGE,"E30");var subQ128=sQuery(id+"F0.wireOp",EDGE,"E29");var subQ129=sQuery(id+"F0.wireOp",EDGE,"E28");var subQ130=sQuery(id+"F0.wireOp",EDGE,"E27");var subQ131=sQuery(id+"F0.wireOp",EDGE,"E26");var subQ132=sQuery(id+"F0.wireOp",EDGE,"E25");var subQ133=sQuery(id+"F0.wireOp",EDGE,"E24");var subQ134=sQuery(id+"F0.wireOp",EDGE,"E10");var subQ135=sQuery(id+"F0.wireOp",EDGE,"E9");var subQ136=sQuery(id+"F0.wireOp",EDGE,"E8");var subQ137=sQuery(id+"F0.wireOp",EDGE,"E7");var subQ138=sQuery(id+"F0.wireOp",EDGE,"E6");var subQ139=sQuery(id+"F0.wireOp",EDGE,"E5");var subQ140=sQuery(id+"F0.wireOp",EDGE,"E11");var subQ141=sQuery(id+"F0.wireOp",EDGE,"E47");var subQ142=sQuery(id+"F0.wireOp",EDGE,"E217");var subQ143=sQuery(id+"F0.wireOp",EDGE,"E216");var subQ144=sQuery(id+"F0.wireOp",EDGE,"E1");var subQ145=sQuery(id+"F0.wireOp",EDGE,"E104");var subQ146=sQuery(id+"F0.wireOp",EDGE,"E23");var subQ147=sQuery(id+"F0.wireOp",EDGE,"E4");var subQ148=sQuery(id+"F0.wireOp",EDGE,"E2");var subQ149=sQuery(id+"F0.wireOp",EDGE,"E3");var subQ150=sQuery(id+"F0.wireOp",EDGE,"E12");var subQ151=sQuery(id+"F0.wireOp",EDGE,"E13");var subQ152=sQuery(id+"F0.wireOp",EDGE,"E14");var subQ153=sQuery(id+"F0.wireOp",EDGE,"E15");var subQ154=sQuery(id+"F0.wireOp",EDGE,"E16");var subQ155=sQuery(id+"F0.wireOp",EDGE,"E17");var subQ156=sQuery(id+"F0.wireOp",EDGE,"E18");var subQ157=sQuery(id+"F0.wireOp",EDGE,"E19");var subQ158=sQuery(id+"F0.wireOp",EDGE,"E20");var subQ159=sQuery(id+"F0.wireOp",EDGE,"E21");var subQ160=sQuery(id+"F0.wireOp",EDGE,"E22");var subQ161=sQuery(id+"F0.wireOp",EDGE,"E48");var subQ162=sQuery(id+"F0.wireOp",EDGE,"E49");var subQ163=sQuery(id+"F0.wireOp",EDGE,"E50");var subQ164=sQuery(id+"F0.wireOp",EDGE,"E51");var subQ165=sQuery(id+"F0.wireOp",EDGE,"E52");var subQ166=sQuery(id+"F0.wireOp",EDGE,"E53");var subQ167=sQuery(id+"F0.wireOp",EDGE,"E54");var subQ168=sQuery(id+"F0.wireOp",EDGE,"E55");var subQ169=sQuery(id+"F0.wireOp",EDGE,"E56");var subQ170=sQuery(id+"F0.wireOp",EDGE,"E58");var subQ171=sQuery(id+"F0.wireOp",EDGE,"E57");var subQ172=sQuery(id+"F0.wireOp",EDGE,"E59");var subQ173=sQuery(id+"F0.wireOp",EDGE,"E60");var subQ174=sQuery(id+"F0.wireOp",EDGE,"E61");var subQ175=sQuery(id+"F0.wireOp",EDGE,"E62");var subQ176=sQuery(id+"F0.wireOp",EDGE,"E63");var subQ177=sQuery(id+"F0.wireOp",EDGE,"E65");var subQ178=sQuery(id+"F0.wireOp",EDGE,"E64");var subQ179=sQuery(id+"F0.wireOp",EDGE,"E66");var subQ180=sQuery(id+"F0.wireOp",EDGE,"E67");var subQ181=sQuery(id+"F0.wireOp",EDGE,"E68");var subQ182=sQuery(id+"F0.wireOp",EDGE,"E69");var subQ183=sQuery(id+"F0.wireOp",EDGE,"E71");var subQ184=sQuery(id+"F0.wireOp",EDGE,"E70");var subQ185=sQuery(id+"F0.wireOp",EDGE,"E72");var subQ186=sQuery(id+"F0.wireOp",EDGE,"E73");var subQ187=sQuery(id+"F0.wireOp",EDGE,"E77");var subQ188=sQuery(id+"F0.wireOp",EDGE,"E76");var subQ189=sQuery(id+"F0.wireOp",EDGE,"E75");var subQ190=sQuery(id+"F0.wireOp",EDGE,"E74");var subQ191=sQuery(id+"F0.wireOp",EDGE,"E79");var subQ192=sQuery(id+"F0.wireOp",EDGE,"E78");var subQ193=sQuery(id+"F0.wireOp",EDGE,"E80");var subQ194=sQuery(id+"F0.wireOp",EDGE,"E81");var subQ195=sQuery(id+"F0.wireOp",EDGE,"E82");var subQ196=sQuery(id+"F0.wireOp",EDGE,"E83");var subQ197=sQuery(id+"F0.wireOp",EDGE,"E84");var subQ198=sQuery(id+"F0.wireOp",EDGE,"E85");var subQ199=sQuery(id+"F0.wireOp",EDGE,"E86");var subQ200=sQuery(id+"F0.wireOp",EDGE,"E87");var subQ201=sQuery(id+"F0.wireOp",EDGE,"E88");var subQ202=sQuery(id+"F0.wireOp",EDGE,"E89");var subQ203=sQuery(id+"F0.wireOp",EDGE,"E90");var subQ204=sQuery(id+"F0.wireOp",EDGE,"E91");var subQ205=sQuery(id+"F0.wireOp",EDGE,"E92");var subQ206=sQuery(id+"F0.wireOp",EDGE,"E93");var subQ207=sQuery(id+"F0.wireOp",EDGE,"E94");var subQ208=sQuery(id+"F0.wireOp",EDGE,"E95");var subQ209=sQuery(id+"F0.wireOp",EDGE,"E96");var subQ210=sQuery(id+"F0.wireOp",EDGE,"E97");var subQ211=sQuery(id+"F0.wireOp",EDGE,"E98");var subQ212=sQuery(id+"F0.wireOp",EDGE,"E99");var subQ213=sQuery(id+"F0.wireOp",EDGE,"E100");var subQ214=sQuery(id+"F0.wireOp",EDGE,"E101");var subQ215=sQuery(id+"F0.wireOp",EDGE,"E102");var subQ216=sQuery(id+"F0.wireOp",EDGE,"E103");var subQ217=sQuery(id+"F0.wireOp",EDGE,"E221");var subQ218=sQuery(id+"F0.wireOp",EDGE,"E220");var subQ219=sQuery(id+"F0.wireOp",EDGE,"E219");var subQ220=sQuery(id+"F0.wireOp",EDGE,"E218");var subQ221=sQuery(id+"F0.wireOp",EDGE,"E222");var subQ222=sQuery(id+"F0.wireOp",EDGE,"E223");var subQ223=sQuery(id+"F0.wireOp",EDGE,"E224");var subQ224=sQuery(id+"F0.wireOp",EDGE,"E225");var subQ225=sQuery(id+"F0.wireOp",EDGE,"E226");var subQ226=sQuery(id+"F0.wireOp",EDGE,"E227");var subQ227=sQuery(id+"F0.wireOp",EDGE,"E228");var subQ228=sQuery(id+"F0.wireOp",EDGE,"E230");var subQ229=sQuery(id+"F0.wireOp",EDGE,"E229");var subQ230=sQuery(id+"F0.wireOp",EDGE,"E231");var subQ231=sQuery(id+"F0.wireOp",EDGE,"E232");var subQ232=sQuery(id+"F0.wireOp",EDGE,"E233");var subQ233=sQuery(id+"F0.wireOp",EDGE,"E234");var subQ234=sQuery(id+"F0.wireOp",EDGE,"E235");var subQ235=sQuery(id+"F0.wireOp",EDGE,"E236");var subQ236=sQuery(id+"F0.wireOp",EDGE,"E237");var subQ237=sQuery(id+"F0.wireOp",EDGE,"E238");var subQ238=sQuery(id+"F0.wireOp",EDGE,"E239");var subQ239=sQuery(id+"F0.wireOp",EDGE,"E240");var subQ240=sQuery(id+"F0.wireOp",EDGE,"E241");var subQ241=sQuery(id+"F0.wireOp",EDGE,"E242");var subQ242=sQuery(id+"F0.wireOp",EDGE,"E243");var subQ243=sQuery(id+"F0.wireOp",EDGE,"E244");var subQ244=sQuery(id+"F0.wireOp",EDGE,"E245");var subQ245=sQuery(id+"F0.wireOp",EDGE,"E246");var subQ246=sQuery(id+"F0.wireOp",EDGE,"E247");var subQ247=sQuery(id+"F0.wireOp",EDGE,"E249");var subQ248=sQuery(id+"F0.wireOp",EDGE,"E248");var subQ249=sQuery(id+"F0.wireOp",EDGE,"E251");var subQ250=sQuery(id+"F0.wireOp",EDGE,"E250");var subQ251=sQuery(id+"F0.wireOp",EDGE,"E252");var subQ252=sQuery(id+"F0.wireOp",EDGE,"E253");Q0=makeQuery(id+"FHQDwOuF6d0dOpx_1.boolean.opBoolean","SPLIT",FACE,{"disambiguationData":[TD([makeQuery(id+"F1.opExtrude","SWEPT_FACE",FACE,{"disambiguationData":[OSD([subQ144])]})])],"derivedFrom":makeQuery(id+"F1.opExtrude","CAP_FACE",FACE,{"disambiguationData":[OSD([subQ144,subQ148,subQ149,subQ147,subQ139,subQ138,subQ137,subQ136,subQ135,subQ134,subQ140,subQ150,subQ151,subQ152,subQ153,subQ154,subQ155,subQ156,subQ157,subQ158,subQ159,subQ160,subQ146,subQ133,subQ132,subQ131,subQ130,subQ129,subQ128,subQ127,subQ126,subQ125,subQ124,subQ123,subQ122,subQ121,subQ120,subQ119,subQ118,subQ117,subQ116,subQ115,subQ114,subQ113,subQ112,subQ111,subQ141,subQ161,subQ162,subQ163,subQ164,subQ165,subQ166,subQ167,subQ168,subQ169,subQ171,subQ170,subQ172,subQ173,subQ174,subQ175,subQ176,subQ178,subQ177,subQ179,subQ180,subQ181,subQ182,subQ184,subQ183,subQ185,subQ186,subQ190,subQ189,subQ188,subQ187,subQ192,subQ191,subQ193,subQ194,subQ195,subQ196,subQ197,subQ198,subQ199,subQ200,subQ201,subQ202,subQ203,subQ204,subQ205,subQ206,subQ207,subQ208,subQ209,subQ210,subQ211,subQ212,subQ213,subQ214,subQ215,subQ216,subQ145,subQ110,subQ109,subQ108,subQ107,subQ106,subQ105,subQ104,subQ103,subQ102,subQ101,subQ100,subQ99,subQ98,subQ97,subQ96,subQ95,subQ94,subQ93,subQ92,subQ91,subQ90,subQ89,subQ88,subQ87,subQ86,subQ85,subQ84,subQ83,subQ82,subQ81,subQ80,subQ79,subQ78,subQ77,subQ76,subQ75,subQ74,subQ73,subQ72,subQ71,subQ70,subQ69,subQ68,subQ67,subQ66,subQ65,subQ64,subQ63,subQ62,subQ61,subQ60,subQ59,subQ58,subQ57,subQ56,subQ55,subQ54,subQ53,subQ52,subQ51,subQ50,subQ49,subQ48,subQ47,subQ46,subQ45,subQ44,subQ43,subQ42,subQ41,subQ40,subQ39,subQ38,subQ37,subQ36,subQ35,subQ34,subQ33,subQ32,subQ31,subQ30,subQ29,subQ28,subQ27,subQ26,subQ25,subQ24,subQ23,subQ22,subQ21,subQ20,subQ19,subQ18,subQ17,subQ16,subQ15,subQ14,subQ13,subQ12,subQ11,subQ10,subQ9,subQ8,subQ7,subQ6,subQ5,subQ4,subQ3,subQ2,subQ1,subQ0,subQ143,subQ142,subQ220,subQ219,subQ218,subQ217,subQ221,subQ222,subQ223,subQ224,subQ225,subQ226,subQ227,subQ229,subQ228,subQ230,subQ231,subQ232,subQ233,subQ234,subQ235,subQ236,subQ237,subQ238,subQ239,subQ240,subQ241,subQ242,subQ243,subQ244,subQ245,subQ246,subQ248,subQ247,subQ250,subQ249,subQ251,subQ252])],"isStart":false})});}
            var sketch = newSketch(context, id + "F2", { "sketchPlane" : qUnion([Q0])});
            skCircle(sketch, "E254", {"center": v(-86.94, 30.04) * mm, "radius": 2.5 * mm});
            skSolve(sketch);
        }
        {
            var Q0;
            Q0=makeQuery(id+"F2.imprint","IMPRINT",FACE,{"disambiguationData":[TD([[makeQuery(id+"F2.imprint","IMPRINT",EDGE,{"derivedFrom":sQuery(id+"F2.wireOp",EDGE,"E254")}),1.0]])]});
            extrude(context, id + "F3", {"entities" : qUnion([Q0]), "operationType" : NewBodyOperationType.REMOVE, "oppositeDirection" : true, "depth" : 25 * mm});
        }
    });
